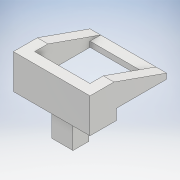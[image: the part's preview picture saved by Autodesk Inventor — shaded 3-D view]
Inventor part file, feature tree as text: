
AUTODESK INVENTOR PART (.ipt)
format: ipt  version: 2018 (Build 220112000, 112)  size: 155,136 bytes
history: native  units: mm
features: extrude x6, sketch x5, plane x1, mirror x1
ambient origin geometry x8: Origin, YZ Plane, XZ Plane, XY Plane, X Axis, Y Axis, Z Axis, Center Point
bodies: Solid1 (feature_tree)
feature tree (13):
  extrude  "Extrusion1"  Depth=10.4mm
  extrude  "Extrusion3"  Depth=1.0mm TaperAngle=0.0deg
  plane  "Work Plane1"
  mirror  "Mirror1"
  extrude  "Extrusion4"  Depth=4.5mm
  sketch  "Sketch6"  dims[d11=1.2mm d12=0.0mm d13=2.0mm d14=0.0mm d15=4.0mm d16=3.0mm d17=2.0mm d18=8.0mm d19=0.0mm d20=2.0mm d21=0.0mm]
  extrude  "Extrusion5"  Depth=2.0mm TaperAngle=0.0deg
  extrude  "Extrusion6"  Depth=2.0mm TaperAngle=0.0deg
  extrude  "Extrusion2"  Depth=4.0mm
  sketch  "Sketch1"  dims[d0=10.4mm d1=10.4mm]
  sketch  "Sketch2"  dims[d2=2.0mm d3=1.0mm d4=0.0mm]
  sketch  "Sketch4"  dims[d5=4.5mm d6=4.5mm]
  sketch  "Sketch5"  dims[d8=2.0mm d9=1.2mm d10=0.0mm]
